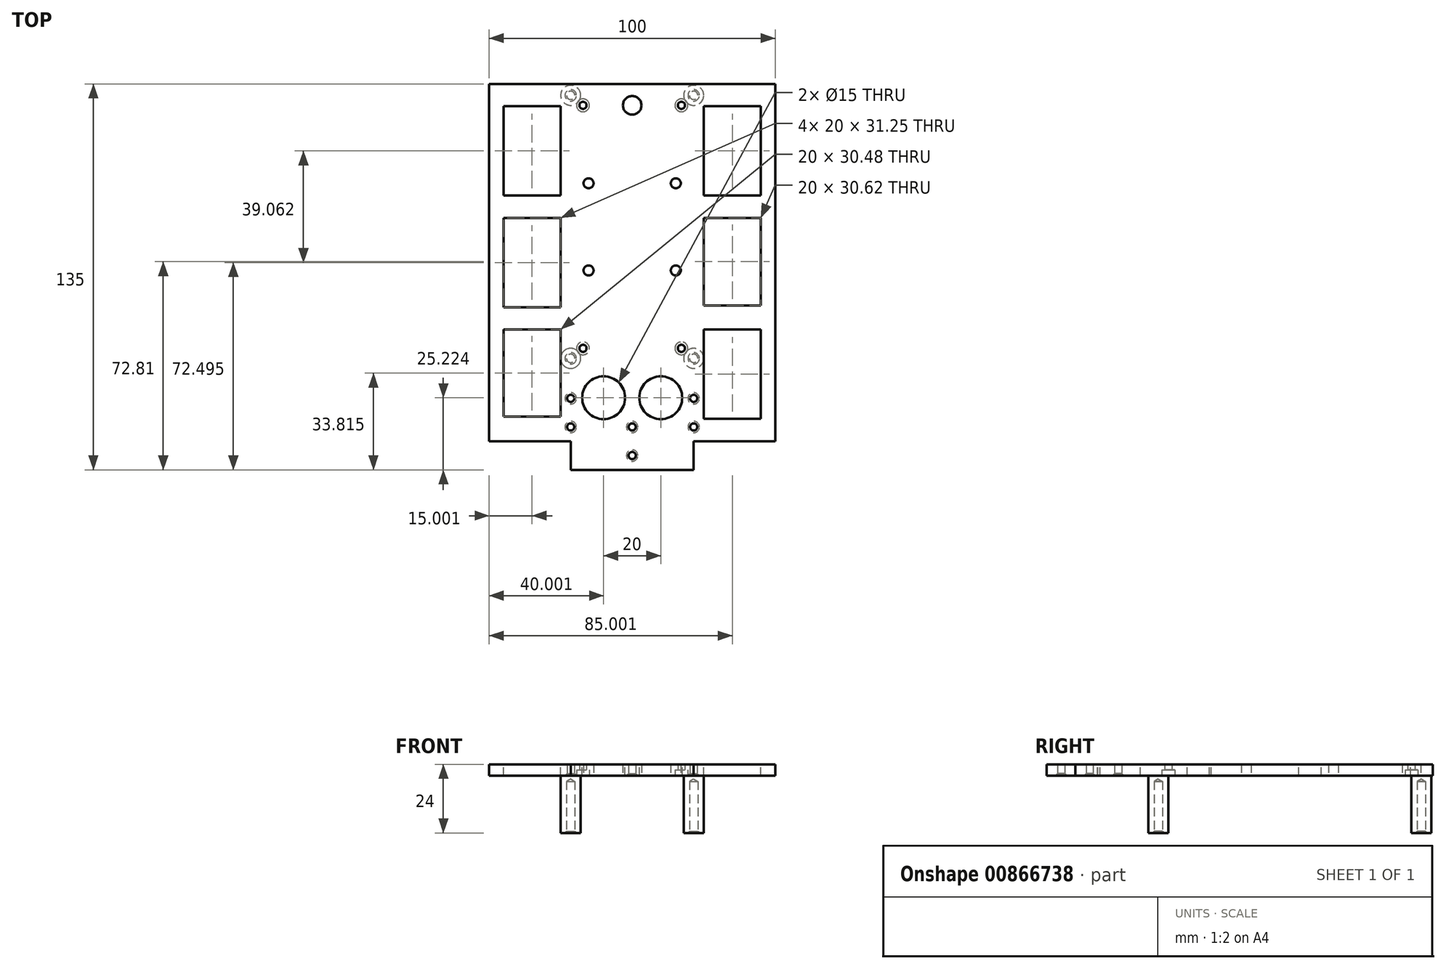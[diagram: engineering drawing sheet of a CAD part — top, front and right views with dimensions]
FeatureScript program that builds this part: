
annotation { "Feature Type Name" : "Feature", "Feature Type Description" : "" }
export const myFeature = defineFeature(function(context is Context, id is Id, definition is map)
    precondition{}
    {
        {
            assignVariable(context, id + "F0", {"name" : "RackThickness", "anyValue" : 4});
        }
        {
            assignVariable(context, id + "F1", {"name" : "PillarHeight", "anyValue" : 20});
        }
        {
            assignVariable(context, id + "F2", {"name" : "TailExtension", "anyValue" : 25});
        }
        {
            assignVariable(context, id + "F3", {"name" : "RackWidthExtension", "anyValue" : 25});
        }
        {
            var Q0;
            Q0=qCreatedBy(makeId("Top.planeOp"),FACE);
            var sketch = newSketch(context, id + "F4", { "sketchPlane" : qUnion([Q0])});
            skLineSegment(sketch, "E0.bottom", {"start": v(-22.43, 77.5) * mm, "end": v(27.57, 77.5) * mm});
            skLineSegment(sketch, "E0.top", {"start": v(-22.43, -22.5) * mm, "end": v(27.57, -22.5) * mm});
            skLineSegment(sketch, "E0.left", {"start": v(-22.43, 77.5) * mm, "end": v(-22.43, -22.5) * mm});
            skLineSegment(sketch, "E0.right", {"start": v(27.57, 77.5) * mm, "end": v(27.57, -22.5) * mm});
            skPoint(sketch, "E1", {"position": v(-14.63, 70) * mm});
            skPoint(sketch, "E2", {"position": v(19.77, 70) * mm});
            skPoint(sketch, "E3", {"position": v(19.77, -15) * mm});
            skPoint(sketch, "E4", {"position": v(-14.63, -15) * mm});
            skPoint(sketch, "E5", {"position": v(-18.93, -18.5) * mm});
            skPoint(sketch, "E6", {"position": v(24.07, -18.5) * mm});
            skPoint(sketch, "E7", {"position": v(24.07, 73.5) * mm});
            skPoint(sketch, "E8", {"position": v(-18.93, 73.5) * mm});
            skCircle(sketch, "E9", {"center": v(-18.93, 73.5) * mm, "radius": 3.5 * mm});
            skCircle(sketch, "E10", {"center": v(-18.93, -18.5) * mm, "radius": 3.5 * mm});
            skCircle(sketch, "E11", {"center": v(24.07, -18.5) * mm, "radius": 3.5 * mm});
            skCircle(sketch, "E12", {"center": v(24.07, 73.5) * mm, "radius": 3.5 * mm});
            skLineSegment(sketch, "E13", {"start": v(-14.63, 70) * mm, "end": v(19.77, -15) * mm});
            skLineSegment(sketch, "E14", {"start": v(-14.63, -15) * mm, "end": v(19.77, 70) * mm});
            skPoint(sketch, "E15", {"position": v(2.57, 27.5) * mm});
            skLineSegment(sketch, "E16.bottom", {"start": v(17.82, 42.75) * mm, "end": v(-12.68, 42.75) * mm});
            skLineSegment(sketch, "E16.top", {"start": v(17.82, 12.25) * mm, "end": v(-12.68, 12.25) * mm});
            skLineSegment(sketch, "E16.left", {"start": v(17.82, 42.75) * mm, "end": v(17.82, 12.25) * mm});
            skLineSegment(sketch, "E16.right", {"start": v(-12.68, 42.75) * mm, "end": v(-12.68, 12.25) * mm});
            skCircle(sketch, "E17", {"center": v(-12.68, 42.75) * mm, "radius": 1.75 * mm});
            skCircle(sketch, "E18", {"center": v(17.82, 42.75) * mm, "radius": 1.75 * mm});
            skCircle(sketch, "E19", {"center": v(-12.68, 12.25) * mm, "radius": 1.75 * mm});
            skCircle(sketch, "E20", {"center": v(17.82, 12.25) * mm, "radius": 1.75 * mm});
            skLineSegment(sketch, "E21", {"start": v(19.77, 70) * mm, "end": v(-14.63, 70) * mm});
            skPoint(sketch, "E22", {"position": v(2.57, 70) * mm});
            skCircle(sketch, "E23", {"center": v(2.57, 70) * mm, "radius": 3.25 * mm});
            skSolve(sketch);
        }
        {
            var Q0;
            Q0=makeQuery(id+"F4.imprint","IMPRINT",FACE,{"disambiguationData":[TD([[makeQuery(id+"F4.imprint","IMPRINT",EDGE,{"derivedFrom":sQuery(id+"F4.wireOp",EDGE,"E0.bottom")}),-1.0]])]});
            var Q1;
            Q1=makeQuery(id+"F4.imprint","IMPRINT",FACE,{"disambiguationData":[TD([[makeQuery(id+"F4.imprint","IMPRINT",EDGE,{"derivedFrom":sQuery(id+"F4.wireOp",EDGE,"E10")}),1.0]])]});
            var Q2;
            Q2=makeQuery(id+"F4.imprint","IMPRINT",FACE,{"disambiguationData":[TD([[makeQuery(id+"F4.imprint","IMPRINT",EDGE,{"derivedFrom":sQuery(id+"F4.wireOp",EDGE,"E11")}),1.0]])]});
            var Q3;
            Q3=makeQuery(id+"F4.imprint","IMPRINT",FACE,{"disambiguationData":[TD([[makeQuery(id+"F4.imprint","IMPRINT",EDGE,{"derivedFrom":sQuery(id+"F4.wireOp",EDGE,"E9")}),1.0]])]});
            var Q4;
            Q4=makeQuery(id+"F4.imprint","IMPRINT",FACE,{"disambiguationData":[TD([[makeQuery(id+"F4.imprint","IMPRINT",EDGE,{"derivedFrom":sQuery(id+"F4.wireOp",EDGE,"E12")}),1.0]])]});
            var Q5;
            {var subQ0=sQuery(id+"F4.wireOp",EDGE,"E16.top");var subQ1=sQuery(id+"F4.wireOp",EDGE,"E13");var subQ2=makeQuery(id+"F4.imprint","INTERSECT",VERTEX,{"derivedFrom":[subQ1,subQ0]});Q5=makeQuery(id+"F4.imprint","IMPRINT",FACE,{"disambiguationData":[TD([[makeQuery(id+"F4.imprint","IMPRINT",EDGE,{"disambiguationData":[TD([[subQ2,1.0]])],"derivedFrom":subQ1}),1.0]])]});}
            var Q6;
            {var subQ5=sQuery(id+"F4.wireOp",EDGE,"E16.bottom");var subQ6=sQuery(id+"F4.wireOp",EDGE,"E13");var subQ7=makeQuery(id+"F4.imprint","INTERSECT",VERTEX,{"derivedFrom":[subQ6,subQ5]});Q6=makeQuery(id+"F4.imprint","IMPRINT",FACE,{"disambiguationData":[TD([[makeQuery(id+"F4.imprint","IMPRINT",EDGE,{"disambiguationData":[TD([[subQ7,-1.0]])],"derivedFrom":subQ6}),-1.0]])]});}
            var Q7;
            {var subQ0=sQuery(id+"F4.wireOp",EDGE,"E16.bottom");var subQ1=sQuery(id+"F4.wireOp",EDGE,"E13");var subQ2=makeQuery(id+"F4.imprint","INTERSECT",VERTEX,{"derivedFrom":[subQ1,subQ0]});Q7=makeQuery(id+"F4.imprint","IMPRINT",FACE,{"disambiguationData":[TD([[makeQuery(id+"F4.imprint","IMPRINT",EDGE,{"disambiguationData":[TD([[subQ2,-1.0]])],"derivedFrom":subQ1}),1.0]])]});}
            var Q8;
            {var subQ0=sQuery(id+"F4.wireOp",EDGE,"E16.top");var subQ1=sQuery(id+"F4.wireOp",EDGE,"E13");var subQ2=makeQuery(id+"F4.imprint","INTERSECT",VERTEX,{"derivedFrom":[subQ1,subQ0]});Q8=makeQuery(id+"F4.imprint","IMPRINT",FACE,{"disambiguationData":[TD([[makeQuery(id+"F4.imprint","IMPRINT",EDGE,{"disambiguationData":[TD([[subQ2,1.0]])],"derivedFrom":subQ1}),-1.0]])]});}
            var Q9;
            {var subQ1=sQuery(id+"F4.wireOp",EDGE,"E13");var subQ5=sQuery(id+"F4.wireOp",EDGE,"E21");var subQ9=makeQuery(id+"F4.imprint","INTERSECT",VERTEX,{"derivedFrom":[subQ1,subQ5]});Q9=makeQuery(id+"F4.imprint","IMPRINT",FACE,{"disambiguationData":[TD([[makeQuery(id+"F4.imprint","IMPRINT",EDGE,{"disambiguationData":[TD([[subQ9,-1.0]])],"derivedFrom":subQ1}),1.0]])]});}
            extrude(context, id + "F5", {"entities" : qUnion([Q0, Q1, Q2, Q3, Q4, Q5, Q6, Q7, Q8, Q9]), "depth" : (getVariable(context, 'RackThickness')) * mm, "offsetDistance" : 25 * mm});
        }
        {
            var Q0;
            Q0=sQuery(id+"F4.wireOp",VERTEX,"E2");
            var Q1;
            Q1=sQuery(id+"F4.wireOp",VERTEX,"E3");
            var Q2;
            Q2=sQuery(id+"F4.wireOp",VERTEX,"E4");
            var Q3;
            Q3=sQuery(id+"F4.wireOp",VERTEX,"E1");
            var Q4;
            Q4=makeQuery(id+"F5.opExtrude","SWEPT_BODY",BODY,{"disambiguationData":[OSD([sQuery(id+"F4.wireOp",EDGE,"E0.bottom"),sQuery(id+"F4.wireOp",EDGE,"E0.top"),sQuery(id+"F4.wireOp",EDGE,"E0.left"),sQuery(id+"F4.wireOp",EDGE,"E0.right")])]});
            hole(context, id + "F6", {"style" : HoleStyle.C_BORE, "endStyle" : HoleEndStyle.THROUGH, "oppositeDirection" : true, "holeDiameter" : 2.5 * mm, "cBoreDiameter" : 4.5 * mm, "cBoreDepth" : 2 * mm, "majorDiameter" : 5 * mm, "isTappedThrough" : true, "tappedDepth" : 12 * mm, "tapClearance" : 3, "startFromSketch" : true, "locations" : qUnion([Q0, Q1, Q2, Q3]), "scope" : qUnion([Q4])});
        }
        {
            var Q0;
            Q0=makeQuery(id+"F4.imprint","IMPRINT",FACE,{"disambiguationData":[TD([[makeQuery(id+"F4.imprint","IMPRINT",EDGE,{"derivedFrom":sQuery(id+"F4.wireOp",EDGE,"E10")}),1.0]])]});
            var Q1;
            Q1=makeQuery(id+"F4.imprint","IMPRINT",FACE,{"disambiguationData":[TD([[makeQuery(id+"F4.imprint","IMPRINT",EDGE,{"derivedFrom":sQuery(id+"F4.wireOp",EDGE,"E11")}),1.0]])]});
            var Q2;
            Q2=makeQuery(id+"F4.imprint","IMPRINT",FACE,{"disambiguationData":[TD([[makeQuery(id+"F4.imprint","IMPRINT",EDGE,{"derivedFrom":sQuery(id+"F4.wireOp",EDGE,"E9")}),1.0]])]});
            var Q3;
            Q3=makeQuery(id+"F4.imprint","IMPRINT",FACE,{"disambiguationData":[TD([[makeQuery(id+"F4.imprint","IMPRINT",EDGE,{"derivedFrom":sQuery(id+"F4.wireOp",EDGE,"E12")}),1.0]])]});
            extrude(context, id + "F7", {"entities" : qUnion([Q0, Q1, Q2, Q3]), "operationType" : NewBodyOperationType.ADD, "oppositeDirection" : true, "depth" : (getVariable(context, 'PillarHeight')) * mm, "offsetDistance" : 25 * mm});
        }
        {
            var Q0;
            Q0=makeQuery(id+"F7.opExtrude","CAP_FACE",FACE,{"disambiguationData":[OSD([sQuery(id+"F4.wireOp",EDGE,"E9")])],"isStart":false});
            var sketch = newSketch(context, id + "F8", { "sketchPlane" : qUnion([Q0])});
            skPoint(sketch, "E24", {"position": v(-18.93, -73.5) * mm});
            skSolve(sketch);
        }
        {
            var Q0;
            Q0=sQuery(id+"F8.wireOp",VERTEX,"E24");
            var Q1;
            Q1=makeQuery(id+"F5.opExtrude","SWEPT_BODY",BODY,{"disambiguationData":[OSD([sQuery(id+"F4.wireOp",EDGE,"E0.bottom"),sQuery(id+"F4.wireOp",EDGE,"E0.top"),sQuery(id+"F4.wireOp",EDGE,"E0.left"),sQuery(id+"F4.wireOp",EDGE,"E0.right")])]});
            hole(context, id + "F9", {"style" : HoleStyle.C_SINK, "endStyle" : HoleEndStyle.BLIND, "holeDiameter" : 2.9 * mm, "cSinkDiameter" : 4 * mm, "cSinkAngle" : 90 * degree, "majorDiameter" : 5 * mm, "holeDepth" : (.9 * getVariable(context, 'PillarHeight')) * mm, "isTappedThrough" : true, "tappedDepth" : 12 * mm, "tapClearance" : 3, "startFromSketch" : true, "locations" : qUnion([Q0]), "scope" : qUnion([Q1])});
        }
        {
            var Q0;
            Q0=makeQuery(id+"F7.opExtrude","CAP_FACE",FACE,{"disambiguationData":[OSD([sQuery(id+"F4.wireOp",EDGE,"E10")])],"isStart":false});
            var sketch = newSketch(context, id + "F10", { "sketchPlane" : qUnion([Q0])});
            skPoint(sketch, "E25", {"position": v(-18.93, 18.5) * mm});
            skSolve(sketch);
        }
        {
            var Q0;
            Q0=sQuery(id+"F10.wireOp",VERTEX,"E25");
            var Q1;
            Q1=makeQuery(id+"F5.opExtrude","SWEPT_BODY",BODY,{"disambiguationData":[OSD([sQuery(id+"F4.wireOp",EDGE,"E0.bottom"),sQuery(id+"F4.wireOp",EDGE,"E0.top"),sQuery(id+"F4.wireOp",EDGE,"E0.left"),sQuery(id+"F4.wireOp",EDGE,"E0.right")])]});
            hole(context, id + "F11", {"style" : HoleStyle.C_SINK, "endStyle" : HoleEndStyle.BLIND, "holeDiameter" : 2.9 * mm, "cSinkDiameter" : 4 * mm, "cSinkAngle" : 90 * degree, "majorDiameter" : 5 * mm, "holeDepth" : (.9 * getVariable(context, 'PillarHeight')) * mm, "isTappedThrough" : true, "tappedDepth" : 12 * mm, "tapClearance" : 3, "startFromSketch" : true, "locations" : qUnion([Q0]), "scope" : qUnion([Q1])});
        }
        {
            var Q0;
            Q0=makeQuery(id+"F7.opExtrude","CAP_FACE",FACE,{"disambiguationData":[OSD([sQuery(id+"F4.wireOp",EDGE,"E12")])],"isStart":false});
            var sketch = newSketch(context, id + "F12", { "sketchPlane" : qUnion([Q0])});
            skPoint(sketch, "E26", {"position": v(24.07, -73.5) * mm});
            skSolve(sketch);
        }
        {
            var Q0;
            Q0=sQuery(id+"F12.wireOp",VERTEX,"E26");
            var Q1;
            Q1=makeQuery(id+"F5.opExtrude","SWEPT_BODY",BODY,{"disambiguationData":[OSD([sQuery(id+"F4.wireOp",EDGE,"E0.bottom"),sQuery(id+"F4.wireOp",EDGE,"E0.top"),sQuery(id+"F4.wireOp",EDGE,"E0.left"),sQuery(id+"F4.wireOp",EDGE,"E0.right")])]});
            hole(context, id + "F13", {"style" : HoleStyle.C_SINK, "endStyle" : HoleEndStyle.BLIND, "holeDiameter" : 2.9 * mm, "cSinkDiameter" : 4 * mm, "cSinkAngle" : 90 * degree, "majorDiameter" : 5 * mm, "holeDepth" : (.9 * getVariable(context, 'PillarHeight')) * mm, "isTappedThrough" : true, "tappedDepth" : 12 * mm, "tapClearance" : 3, "startFromSketch" : true, "locations" : qUnion([Q0]), "scope" : qUnion([Q1])});
        }
        {
            var Q0;
            Q0=makeQuery(id+"F7.opExtrude","CAP_FACE",FACE,{"disambiguationData":[OSD([sQuery(id+"F4.wireOp",EDGE,"E11")])],"isStart":false});
            var sketch = newSketch(context, id + "F14", { "sketchPlane" : qUnion([Q0])});
            skPoint(sketch, "E27", {"position": v(24.07, 18.5) * mm});
            skSolve(sketch);
        }
        {
            var Q0;
            Q0=sQuery(id+"F14.wireOp",VERTEX,"E27");
            var Q1;
            Q1=makeQuery(id+"F5.opExtrude","SWEPT_BODY",BODY,{"disambiguationData":[OSD([sQuery(id+"F4.wireOp",EDGE,"E0.bottom"),sQuery(id+"F4.wireOp",EDGE,"E0.top"),sQuery(id+"F4.wireOp",EDGE,"E0.left"),sQuery(id+"F4.wireOp",EDGE,"E0.right")])]});
            hole(context, id + "F15", {"style" : HoleStyle.C_SINK, "endStyle" : HoleEndStyle.BLIND, "holeDiameter" : 2.9 * mm, "cSinkDiameter" : 4 * mm, "cSinkAngle" : 90 * degree, "majorDiameter" : 5 * mm, "holeDepth" : (.9 * getVariable(context, 'PillarHeight')) * mm, "isTappedThrough" : true, "tappedDepth" : 12 * mm, "tapClearance" : 3, "startFromSketch" : true, "locations" : qUnion([Q0]), "scope" : qUnion([Q1])});
        }
        {
            var Q0;
            Q0=makeQuery(id+"F5.opExtrude","SWEPT_FACE",FACE,{"disambiguationData":[OSD([sQuery(id+"F4.wireOp",EDGE,"E0.top")])]});
            extrude(context, id + "F16", {"entities" : qUnion([Q0]), "operationType" : NewBodyOperationType.ADD, "depth" : (getVariable(context, 'TailExtension')) * mm, "offsetDistance" : 25 * mm});
        }
        {
            var Q0;
            {var subQ0=sQuery(id+"F4.wireOp",EDGE,"E0.top");Q0=makeQuery(id+"F16.boolean.opBoolean","MERGE",FACE,{"derivedFrom":[makeQuery(id+"F5.opExtrude","CAP_FACE",FACE,{"disambiguationData":[OSD([sQuery(id+"F4.wireOp",EDGE,"E0.bottom"),subQ0,sQuery(id+"F4.wireOp",EDGE,"E0.left"),sQuery(id+"F4.wireOp",EDGE,"E0.right")])],"isStart":false}),makeQuery(id+"F16.opExtrude","SWEPT_FACE",FACE,{"disambiguationData":[OSD([subQ0]),TDD([makeQuery(id+"F5.opExtrude","CAP_EDGE",EDGE,{"disambiguationData":[OSD([subQ0])],"isStart":false})])]})]});}
            var sketch = newSketch(context, id + "F17", { "sketchPlane" : qUnion([Q0])});
            skLineSegment(sketch, "E28.bottom", {"start": v(22.57, -42.5) * mm, "end": v(-17.43, -42.5) * mm});
            skLineSegment(sketch, "E28.top", {"start": v(22.57, -22.05) * mm, "end": v(-17.43, -22.05) * mm});
            skLineSegment(sketch, "E28.left", {"start": v(22.57, -42.5) * mm, "end": v(22.57, -22.05) * mm});
            skLineSegment(sketch, "E28.right", {"start": v(-17.43, -42.5) * mm, "end": v(-17.43, -22.05) * mm});
            skPoint(sketch, "E29", {"position": v(2.57, -47.5) * mm});
            skPoint(sketch, "E30", {"position": v(2.57, -42.5) * mm});
            skLineSegment(sketch, "E31", {"start": v(2.57, -47.5) * mm, "end": v(2.57, -42.5) * mm});
            skPoint(sketch, "E32", {"position": v(2.57, -45) * mm});
            skCircle(sketch, "E33", {"center": v(2.57, -45) * mm, "radius": 1.25 * mm});
            skPoint(sketch, "E34", {"position": v(2.57, -22.05) * mm});
            skLineSegment(sketch, "E35", {"start": v(2.57, -22.05) * mm, "end": v(2.57, -42.5) * mm, "construction": true});
            skPoint(sketch, "E36", {"position": v(2.57, -32.28) * mm});
            skPoint(sketch, "E37", {"position": v(22.57, -32.28) * mm});
            skPoint(sketch, "E38", {"position": v(-17.43, -32.28) * mm});
            skLineSegment(sketch, "E39", {"start": v(22.57, -32.28) * mm, "end": v(2.57, -32.28) * mm, "construction": true});
            skPoint(sketch, "E40", {"position": v(12.57, -32.28) * mm});
            skLineSegment(sketch, "E41", {"start": v(2.57, -32.28) * mm, "end": v(-17.43, -32.28) * mm, "construction": true});
            skPoint(sketch, "E42", {"position": v(-7.43, -32.28) * mm});
            skCircle(sketch, "E43", {"center": v(12.57, -32.28) * mm, "radius": 7.5 * mm});
            skCircle(sketch, "E44", {"center": v(-7.43, -32.28) * mm, "radius": 7.5 * mm});
            skSolve(sketch);
        }
        {
            var Q0;
            {var subQ0=sQuery(id+"F4.wireOp",EDGE,"E0.right");Q0=makeQuery(id+"F16.boolean.opBoolean","MERGE",FACE,{"derivedFrom":[makeQuery(id+"F5.opExtrude","SWEPT_FACE",FACE,{"disambiguationData":[OSD([subQ0])]}),makeQuery(id+"F16.opExtrude","SWEPT_FACE",FACE,{"disambiguationData":[OSD([sQuery(id+"F4.wireOp",EDGE,"E0.top"),subQ0])]})]});}
            extrude(context, id + "F18", {"entities" : qUnion([Q0]), "operationType" : NewBodyOperationType.ADD, "depth" : (getVariable(context, 'RackWidthExtension')) * mm, "offsetDistance" : 25 * mm});
        }
        {
            var Q0;
            {var subQ0=sQuery(id+"F4.wireOp",EDGE,"E0.left");Q0=makeQuery(id+"F16.boolean.opBoolean","MERGE",FACE,{"derivedFrom":[makeQuery(id+"F5.opExtrude","SWEPT_FACE",FACE,{"disambiguationData":[OSD([subQ0])]}),makeQuery(id+"F16.opExtrude","SWEPT_FACE",FACE,{"disambiguationData":[OSD([sQuery(id+"F4.wireOp",EDGE,"E0.top"),subQ0])]})]});}
            extrude(context, id + "F19", {"entities" : qUnion([Q0]), "operationType" : NewBodyOperationType.ADD, "depth" : (getVariable(context, 'RackWidthExtension')) * mm, "offsetDistance" : 25 * mm});
        }
        {
            var Q0;
            {var subQ0=sQuery(id+"F4.wireOp",EDGE,"E0.left");var subQ1=sQuery(id+"F4.wireOp",EDGE,"E0.top");var subQ2=sQuery(id+"F4.wireOp",EDGE,"E0.right");Q0=makeQuery(id+"F19.boolean.opBoolean","MERGE",FACE,{"derivedFrom":[makeQuery(id+"F18.boolean.opBoolean","MERGE",FACE,{"derivedFrom":[makeQuery(id+"F16.boolean.opBoolean","MERGE",FACE,{"derivedFrom":[makeQuery(id+"F5.opExtrude","CAP_FACE",FACE,{"disambiguationData":[OSD([sQuery(id+"F4.wireOp",EDGE,"E0.bottom"),subQ1,subQ0,subQ2])],"isStart":false}),makeQuery(id+"F16.opExtrude","SWEPT_FACE",FACE,{"disambiguationData":[OSD([subQ1]),TDD([makeQuery(id+"F5.opExtrude","CAP_EDGE",EDGE,{"disambiguationData":[OSD([subQ1])],"isStart":false})])]})]}),makeQuery(id+"F18.opExtrude","SWEPT_FACE",FACE,{"disambiguationData":[OSD([subQ1,subQ2]),TDD([makeQuery(id+"F16.boolean.opBoolean","MERGE",EDGE,{"derivedFrom":[makeQuery(id+"F5.opExtrude","CAP_EDGE",EDGE,{"disambiguationData":[OSD([subQ2])],"isStart":false}),makeQuery(id+"F16.opExtrude","SWEPT_EDGE",EDGE,{"disambiguationData":[OSD([subQ1,subQ2]),TDD([makeQuery(id+"F5.opExtrude","CAP_VERTEX",VERTEX,{"disambiguationData":[OSD([subQ1,subQ2])],"isStart":false})])]})]})])]})]}),makeQuery(id+"F19.opExtrude","SWEPT_FACE",FACE,{"disambiguationData":[OSD([subQ1,subQ0]),TDD([makeQuery(id+"F16.boolean.opBoolean","MERGE",EDGE,{"derivedFrom":[makeQuery(id+"F5.opExtrude","CAP_EDGE",EDGE,{"disambiguationData":[OSD([subQ0])],"isStart":false}),makeQuery(id+"F16.opExtrude","SWEPT_EDGE",EDGE,{"disambiguationData":[OSD([subQ1,subQ0]),TDD([makeQuery(id+"F5.opExtrude","CAP_VERTEX",VERTEX,{"disambiguationData":[OSD([subQ1,subQ0])],"isStart":false})])]})]})])]})]});}
            var sketch = newSketch(context, id + "F20", { "sketchPlane" : qUnion([Q0])});
            skLineSegment(sketch, "E45.bottom", {"start": v(-42.43, 69.68) * mm, "end": v(-22.43, 69.68) * mm});
            skLineSegment(sketch, "E45.top", {"start": v(-42.43, 38.43) * mm, "end": v(-22.43, 38.43) * mm});
            skLineSegment(sketch, "E45.left", {"start": v(-42.43, 69.68) * mm, "end": v(-42.43, 38.43) * mm});
            skLineSegment(sketch, "E45.right", {"start": v(-22.43, 69.68) * mm, "end": v(-22.43, 38.43) * mm});
            skLineSegment(sketch, "E46.bottom", {"start": v(-42.43, 30.62) * mm, "end": v(-22.43, 30.62) * mm});
            skLineSegment(sketch, "E46.top", {"start": v(-42.43, -0.63) * mm, "end": v(-22.43, -0.63) * mm});
            skLineSegment(sketch, "E46.left", {"start": v(-42.43, 30.62) * mm, "end": v(-42.43, -0.63) * mm});
            skLineSegment(sketch, "E46.right", {"start": v(-22.43, 30.62) * mm, "end": v(-22.43, -0.63) * mm});
            skLineSegment(sketch, "E47.bottom", {"start": v(-42.43, -8.44) * mm, "end": v(-22.43, -8.44) * mm});
            skLineSegment(sketch, "E47.top", {"start": v(-42.43, -38.93) * mm, "end": v(-22.43, -38.93) * mm});
            skLineSegment(sketch, "E47.left", {"start": v(-42.43, -8.44) * mm, "end": v(-42.43, -38.93) * mm});
            skLineSegment(sketch, "E47.right", {"start": v(-22.43, -8.44) * mm, "end": v(-22.43, -38.93) * mm});
            skLineSegment(sketch, "E48.bottom", {"start": v(47.57, 69.68) * mm, "end": v(27.57, 69.68) * mm});
            skLineSegment(sketch, "E48.top", {"start": v(47.57, 38.43) * mm, "end": v(27.57, 38.43) * mm});
            skLineSegment(sketch, "E48.left", {"start": v(47.57, 69.68) * mm, "end": v(47.57, 38.43) * mm});
            skLineSegment(sketch, "E48.right", {"start": v(27.57, 69.68) * mm, "end": v(27.57, 38.43) * mm});
            skLineSegment(sketch, "E49.bottom", {"start": v(27.57, 30.62) * mm, "end": v(47.57, 30.62) * mm});
            skLineSegment(sketch, "E49.top", {"start": v(27.57, 0) * mm, "end": v(47.57, 0) * mm});
            skLineSegment(sketch, "E49.left", {"start": v(27.57, 30.62) * mm, "end": v(27.57, 0) * mm});
            skLineSegment(sketch, "E49.right", {"start": v(47.57, 30.62) * mm, "end": v(47.57, 0) * mm});
            skLineSegment(sketch, "E50.bottom", {"start": v(27.57, -8.44) * mm, "end": v(47.57, -8.44) * mm});
            skLineSegment(sketch, "E50.top", {"start": v(27.57, -39.7) * mm, "end": v(47.57, -39.7) * mm});
            skLineSegment(sketch, "E50.left", {"start": v(27.57, -8.44) * mm, "end": v(27.57, -39.7) * mm});
            skLineSegment(sketch, "E50.right", {"start": v(47.57, -8.44) * mm, "end": v(47.57, -39.7) * mm});
            skSolve(sketch);
        }
        {
            var Q0;
            Q0=makeQuery(id+"F20.imprint","IMPRINT",FACE,{"disambiguationData":[TD([[makeQuery(id+"F20.imprint","IMPRINT",EDGE,{"derivedFrom":sQuery(id+"F20.wireOp",EDGE,"E47.bottom")}),-1.0]])]});
            var Q1;
            Q1=makeQuery(id+"F20.imprint","IMPRINT",FACE,{"disambiguationData":[TD([[makeQuery(id+"F20.imprint","IMPRINT",EDGE,{"derivedFrom":sQuery(id+"F20.wireOp",EDGE,"E46.bottom")}),-1.0]])]});
            var Q2;
            Q2=makeQuery(id+"F20.imprint","IMPRINT",FACE,{"disambiguationData":[TD([[makeQuery(id+"F20.imprint","IMPRINT",EDGE,{"derivedFrom":sQuery(id+"F20.wireOp",EDGE,"E45.bottom")}),-1.0]])]});
            var Q3;
            Q3=makeQuery(id+"F20.imprint","IMPRINT",FACE,{"disambiguationData":[TD([[makeQuery(id+"F20.imprint","IMPRINT",EDGE,{"derivedFrom":sQuery(id+"F20.wireOp",EDGE,"E48.bottom")}),1.0]])]});
            var Q4;
            Q4=makeQuery(id+"F20.imprint","IMPRINT",FACE,{"disambiguationData":[TD([[makeQuery(id+"F20.imprint","IMPRINT",EDGE,{"derivedFrom":sQuery(id+"F20.wireOp",EDGE,"E49.bottom")}),-1.0]])]});
            var Q5;
            Q5=makeQuery(id+"F20.imprint","IMPRINT",FACE,{"disambiguationData":[TD([[makeQuery(id+"F20.imprint","IMPRINT",EDGE,{"derivedFrom":sQuery(id+"F20.wireOp",EDGE,"E50.bottom")}),-1.0]])]});
            extrude(context, id + "F21", {"entities" : qUnion([Q0, Q1, Q2, Q3, Q4, Q5]), "operationType" : NewBodyOperationType.REMOVE, "oppositeDirection" : true, "depth" : (getVariable(context, 'RackThickness')) * mm, "offsetDistance" : 25 * mm});
        }
        {
            var Q0;
            Q0=makeQuery(id+"F17.imprint","IMPRINT",FACE,{"disambiguationData":[TD([[makeQuery(id+"F17.imprint","IMPRINT",EDGE,{"derivedFrom":sQuery(id+"F17.wireOp",EDGE,"E44")}),1.0]])]});
            var Q1;
            Q1=makeQuery(id+"F17.imprint","IMPRINT",FACE,{"disambiguationData":[TD([[makeQuery(id+"F17.imprint","IMPRINT",EDGE,{"derivedFrom":sQuery(id+"F17.wireOp",EDGE,"E43")}),1.0]])]});
            extrude(context, id + "F22", {"entities" : qUnion([Q0, Q1]), "operationType" : NewBodyOperationType.REMOVE, "oppositeDirection" : true, "depth" : (getVariable(context, 'RackThickness')) * mm, "offsetDistance" : 25 * mm});
        }
        {
            var Q0;
            {var subQ0=sQuery(id+"F4.wireOp",EDGE,"E0.left");var subQ1=sQuery(id+"F4.wireOp",EDGE,"E0.top");var subQ2=sQuery(id+"F4.wireOp",EDGE,"E0.right");Q0=makeQuery(id+"F19.boolean.opBoolean","MERGE",FACE,{"derivedFrom":[makeQuery(id+"F18.boolean.opBoolean","MERGE",FACE,{"derivedFrom":[makeQuery(id+"F16.opExtrude","CAP_FACE",FACE,{"disambiguationData":[OSD([subQ1])],"isStart":false}),makeQuery(id+"F18.opExtrude","SWEPT_FACE",FACE,{"disambiguationData":[OSD([subQ1,subQ2]),TDD([makeQuery(id+"F16.opExtrude","CAP_EDGE",EDGE,{"disambiguationData":[OSD([subQ1,subQ2])],"isStart":false})])]})]}),makeQuery(id+"F19.opExtrude","SWEPT_FACE",FACE,{"disambiguationData":[OSD([subQ1,subQ0]),TDD([makeQuery(id+"F16.opExtrude","CAP_EDGE",EDGE,{"disambiguationData":[OSD([subQ1,subQ0])],"isStart":false})])]})]});}
            var sketch = newSketch(context, id + "F23", { "sketchPlane" : qUnion([Q0])});
            skPoint(sketch, "E51", {"position": v(2.57, 4) * mm});
            skPoint(sketch, "E52", {"position": v(2.57, 0) * mm});
            skLineSegment(sketch, "E53", {"start": v(2.57, 4) * mm, "end": v(2.57, 0) * mm, "construction": true});
            skPoint(sketch, "E54", {"position": v(2.57, 2) * mm});
            skLineSegment(sketch, "E55.bottom", {"start": v(24.07, 0) * mm, "end": v(-18.93, 0) * mm, "construction": true});
            skLineSegment(sketch, "E55.top", {"start": v(24.07, 4) * mm, "end": v(-18.93, 4) * mm, "construction": true});
            skLineSegment(sketch, "E55.left", {"start": v(24.07, 0) * mm, "end": v(24.07, 4) * mm, "construction": true});
            skLineSegment(sketch, "E55.right", {"start": v(-18.93, 0) * mm, "end": v(-18.93, 4) * mm, "construction": true});
            skLineSegment(sketch, "E56.bottom", {"start": v(24.07, 4) * mm, "end": v(-18.93, 4) * mm});
            skLineSegment(sketch, "E56.top", {"start": v(24.07, 0) * mm, "end": v(-18.93, 0) * mm});
            skLineSegment(sketch, "E56.left", {"start": v(24.07, 4) * mm, "end": v(24.07, 0) * mm});
            skLineSegment(sketch, "E56.right", {"start": v(-18.93, 4) * mm, "end": v(-18.93, 0) * mm});
            skSolve(sketch);
        }
        {
            var Q0;
            Q0=makeQuery(id+"F23.imprint","IMPRINT",FACE,{"disambiguationData":[TD([[makeQuery(id+"F23.imprint","IMPRINT",EDGE,{"derivedFrom":sQuery(id+"F23.wireOp",EDGE,"E56.bottom")}),-1.0]])]});
            extrude(context, id + "F24", {"entities" : qUnion([Q0]), "operationType" : NewBodyOperationType.ADD, "depth" : 10 * mm, "offsetDistance" : 25 * mm});
        }
        {
            var Q0;
            {var subQ0=sQuery(id+"F4.wireOp",EDGE,"E0.left");var subQ1=sQuery(id+"F4.wireOp",EDGE,"E0.top");var subQ2=sQuery(id+"F4.wireOp",EDGE,"E0.right");var subQ3=sQuery(id+"F4.wireOp",EDGE,"E0.bottom");var subQ4=makeQuery(id+"F5.opExtrude","CAP_FACE",FACE,{"disambiguationData":[OSD([subQ3,subQ1,subQ0,subQ2])],"isStart":true});var subQ5=makeQuery(id+"F5.opExtrude","SWEPT_FACE",FACE,{"disambiguationData":[OSD([subQ1])]});var subQ6=makeQuery(id+"F5.opExtrude","SWEPT_FACE",FACE,{"disambiguationData":[OSD([subQ0])]});var subQ7=makeQuery(id+"F7.opExtrude","SWEPT_FACE",FACE,{"disambiguationData":[OSD([sQuery(id+"F4.wireOp",EDGE,"E10")])]});var subQ8=makeQuery(id+"F5.opExtrude","CAP_EDGE",EDGE,{"disambiguationData":[OSD([subQ0])],"isStart":true});var subQ9=makeQuery(id+"F7.opExtrude","SWEPT_FACE",FACE,{"disambiguationData":[OSD([sQuery(id+"F4.wireOp",EDGE,"E9")])]});var subQ10=makeQuery(id+"F5.opExtrude","SWEPT_FACE",FACE,{"disambiguationData":[OSD([subQ3])]});var subQ11=makeQuery(id+"F5.opExtrude","SWEPT_FACE",FACE,{"disambiguationData":[OSD([subQ2])]});var subQ12=makeQuery(id+"F7.opExtrude","SWEPT_FACE",FACE,{"disambiguationData":[OSD([sQuery(id+"F4.wireOp",EDGE,"E11")])]});var subQ13=makeQuery(id+"F5.opExtrude","CAP_EDGE",EDGE,{"disambiguationData":[OSD([subQ2])],"isStart":true});var subQ14=makeQuery(id+"F7.opExtrude","SWEPT_FACE",FACE,{"disambiguationData":[OSD([sQuery(id+"F4.wireOp",EDGE,"E12")])]});Q0=makeQuery(id+"F24.boolean.opBoolean","MERGE",FACE,{"derivedFrom":[makeQuery(id+"F19.boolean.opBoolean","MERGE",FACE,{"derivedFrom":[makeQuery(id+"F18.boolean.opBoolean","MERGE",FACE,{"derivedFrom":[makeQuery(id+"F16.boolean.opBoolean","MERGE",FACE,{"derivedFrom":[subQ4,makeQuery(id+"F16.opExtrude","SWEPT_FACE",FACE,{"disambiguationData":[OSD([subQ1]),TDD([makeQuery(id+"F5.opExtrude","CAP_EDGE",EDGE,{"disambiguationData":[OSD([subQ1])],"isStart":true})])]})]}),makeQuery(id+"F18.opExtrude","SWEPT_FACE",FACE,{"disambiguationData":[OSD([subQ1,subQ2]),TDD([makeQuery(id+"F7.boolean.opBoolean","SPLIT",EDGE,{"disambiguationData":[TD([subQ10,subQ4,subQ11,subQ14])],"derivedFrom":subQ13}),makeQuery(id+"F7.boolean.opBoolean","SPLIT",EDGE,{"disambiguationData":[TD([subQ4,subQ11,subQ12,subQ14])],"derivedFrom":subQ13}),makeQuery(id+"F16.boolean.opBoolean","MERGE",EDGE,{"derivedFrom":[makeQuery(id+"F7.boolean.opBoolean","SPLIT",EDGE,{"disambiguationData":[TD([subQ4,subQ5,subQ11,subQ12])],"derivedFrom":subQ13}),makeQuery(id+"F16.opExtrude","SWEPT_EDGE",EDGE,{"disambiguationData":[OSD([subQ1,subQ2]),TDD([makeQuery(id+"F5.opExtrude","CAP_VERTEX",VERTEX,{"disambiguationData":[OSD([subQ1,subQ2])],"isStart":true})])]})]})])]})]}),makeQuery(id+"F19.opExtrude","SWEPT_FACE",FACE,{"disambiguationData":[OSD([subQ1,subQ0]),TDD([makeQuery(id+"F7.boolean.opBoolean","SPLIT",EDGE,{"disambiguationData":[TD([subQ10,subQ4,subQ6,subQ9])],"derivedFrom":subQ8}),makeQuery(id+"F7.boolean.opBoolean","SPLIT",EDGE,{"disambiguationData":[TD([subQ4,subQ6,subQ9,subQ7])],"derivedFrom":subQ8}),makeQuery(id+"F16.boolean.opBoolean","MERGE",EDGE,{"derivedFrom":[makeQuery(id+"F7.boolean.opBoolean","SPLIT",EDGE,{"disambiguationData":[TD([subQ4,subQ5,subQ6,subQ7])],"derivedFrom":subQ8}),makeQuery(id+"F16.opExtrude","SWEPT_EDGE",EDGE,{"disambiguationData":[OSD([subQ1,subQ0]),TDD([makeQuery(id+"F5.opExtrude","CAP_VERTEX",VERTEX,{"disambiguationData":[OSD([subQ1,subQ0])],"isStart":true})])]})]})])]})]}),makeQuery(id+"F24.opExtrude","SWEPT_FACE",FACE,{"disambiguationData":[OSD([sQuery(id+"F23.wireOp",EDGE,"E56.top")])]})]});}
            var sketch = newSketch(context, id + "F25", { "sketchPlane" : qUnion([Q0])});
            skPoint(sketch, "E57", {"position": v(2.57, 57.5) * mm});
            skPoint(sketch, "E58", {"position": v(2.57, 42.5) * mm});
            skLineSegment(sketch, "E59", {"start": v(2.57, 57.5) * mm, "end": v(2.57, 42.5) * mm});
            skPoint(sketch, "E60", {"position": v(2.57, 52.5) * mm});
            skPoint(sketch, "E61", {"position": v(2.57, 47.5) * mm});
            skLineSegment(sketch, "E62", {"start": v(-18.93, 47.5) * mm, "end": v(-18.93, 32.5) * mm});
            skLineSegment(sketch, "E63", {"start": v(-18.93, 32.5) * mm, "end": v(-18.93, 42.5) * mm});
            skLineSegment(sketch, "E64", {"start": v(24.07, 47.5) * mm, "end": v(24.07, 32.5) * mm});
            skLineSegment(sketch, "E65", {"start": v(24.07, 32.5) * mm, "end": v(24.07, 42.5) * mm});
            skSolve(sketch);
        }
        {
            var Q0;
            Q0=sQuery(id+"F25.wireOp",VERTEX,"E60");
            var Q1;
            Q1=sQuery(id+"F25.wireOp",VERTEX,"E58");
            var Q2;
            Q2=makeQuery(id+"F5.opExtrude","SWEPT_BODY",BODY,{"disambiguationData":[OSD([sQuery(id+"F4.wireOp",EDGE,"E0.bottom"),sQuery(id+"F4.wireOp",EDGE,"E0.top"),sQuery(id+"F4.wireOp",EDGE,"E0.left"),sQuery(id+"F4.wireOp",EDGE,"E0.right")])]});
            hole(context, id + "F26", {"style" : HoleStyle.C_SINK, "endStyle" : HoleEndStyle.BLIND, "holeDiameter" : 2.5 * mm, "cSinkDiameter" : 4 * mm, "cSinkAngle" : 90 * degree, "majorDiameter" : 5 * mm, "holeDepth" : 15 * mm, "isTappedThrough" : true, "tappedDepth" : 12 * mm, "tapClearance" : 3, "startFromSketch" : true, "locations" : qUnion([Q0, Q1]), "scope" : qUnion([Q2])});
        }
        {
            var Q0;
            Q0=sQuery(id+"F25.wireOp",VERTEX,"E63.end");
            var Q1;
            Q1=sQuery(id+"F25.wireOp",VERTEX,"E62.end");
            var Q2;
            Q2=sQuery(id+"F25.wireOp",VERTEX,"E64.end");
            var Q3;
            Q3=sQuery(id+"F25.wireOp",VERTEX,"E65.end");
            var Q4;
            Q4=makeQuery(id+"F5.opExtrude","SWEPT_BODY",BODY,{"disambiguationData":[OSD([sQuery(id+"F4.wireOp",EDGE,"E0.bottom"),sQuery(id+"F4.wireOp",EDGE,"E0.top"),sQuery(id+"F4.wireOp",EDGE,"E0.left"),sQuery(id+"F4.wireOp",EDGE,"E0.right")])]});
            hole(context, id + "F27", {"style" : HoleStyle.C_SINK, "endStyle" : HoleEndStyle.BLIND, "holeDiameter" : 2.5 * mm, "cSinkDiameter" : 4 * mm, "cSinkAngle" : 90 * degree, "majorDiameter" : 5 * mm, "holeDepth" : 15 * mm, "isTappedThrough" : true, "tappedDepth" : 12 * mm, "tapClearance" : 3, "startFromSketch" : true, "locations" : qUnion([Q0, Q1, Q2, Q3]), "scope" : qUnion([Q4])});
        }
    });
